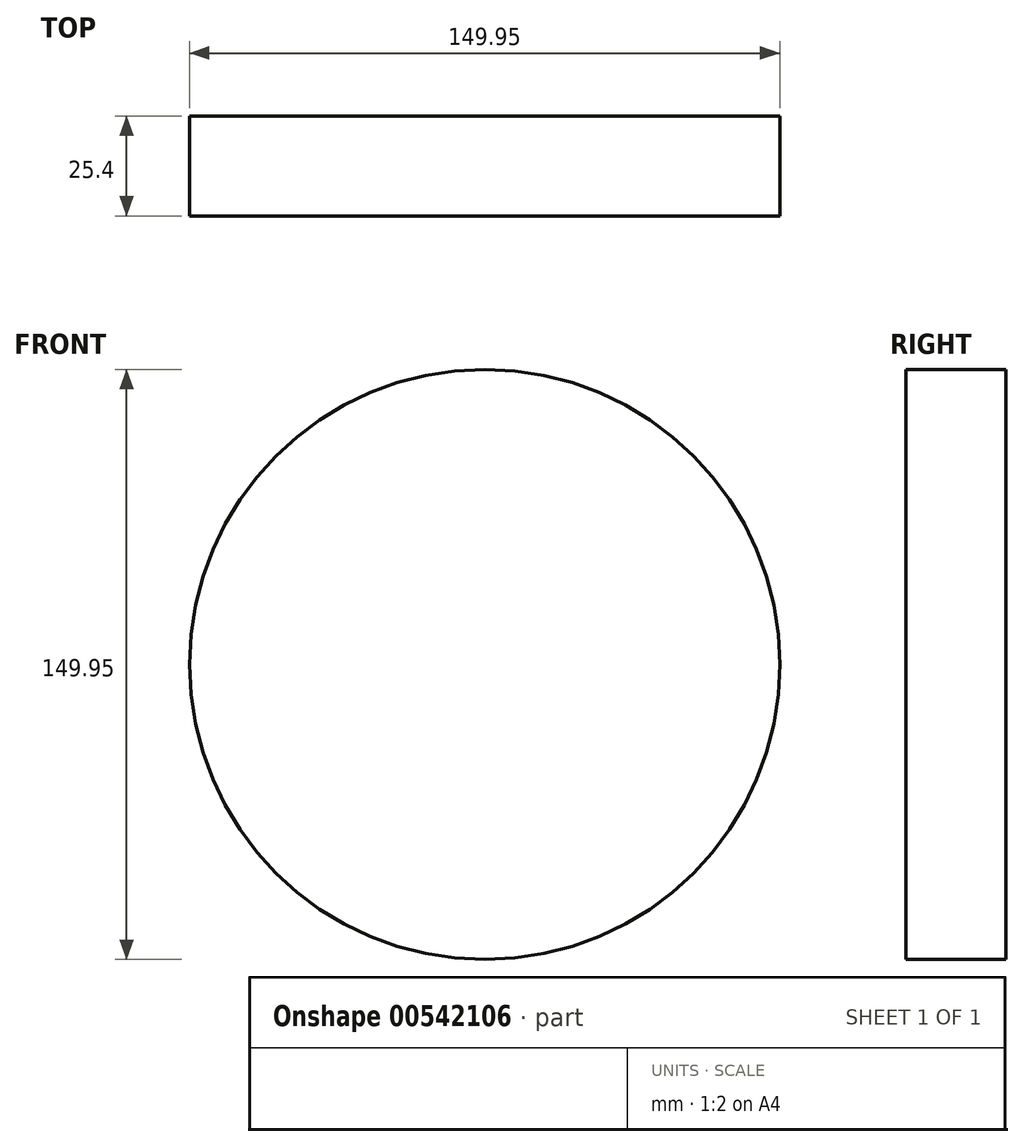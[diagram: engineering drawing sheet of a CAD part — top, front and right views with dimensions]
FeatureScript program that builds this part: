
annotation { "Feature Type Name" : "Feature", "Feature Type Description" : "" }
export const myFeature = defineFeature(function(context is Context, id is Id, definition is map)
    precondition{}
    {
        {
            var Q0;
            Q0=qCreatedBy(makeId("Front.planeOp"),FACE);
            var sketch = newSketch(context, id + "F0", { "sketchPlane" : qUnion([Q0])});
            skCircle(sketch, "E0", {"center": v(-1.37, 0.93) * mm, "radius": 74.98 * mm});
            skSolve(sketch);
        }
        {
            var Q0;
            Q0=makeQuery(id+"F0.imprint","IMPRINT",FACE,{"disambiguationData":[TD([[makeQuery(id+"F0.imprint","IMPRINT",EDGE,{"derivedFrom":sQuery(id+"F0.wireOp",EDGE,"E0")}),1.0]])]});
            extrude(context, id + "F1", {"entities" : qUnion([Q0]), "depth" : 25.4 * mm, "offsetDistance" : 25.4 * mm});
        }
    });
